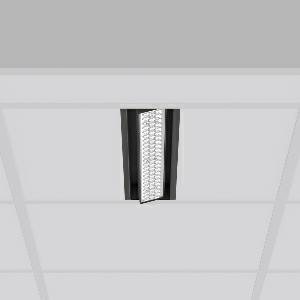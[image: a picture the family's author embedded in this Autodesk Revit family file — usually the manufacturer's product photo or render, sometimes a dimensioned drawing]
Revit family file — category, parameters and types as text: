
# Revit family: tx-move_901725_003_1_76_cce0
name_source: partatom
category: Lighting Fixtures
units: mm (PartAtom-declared; Revit-internal decimal feet)

## family parameters
Cut with Voids When Loaded = No
Host = Face
Light Source = No
Part Type = Normal
Room Calculation Point = No
Round Connector Dimension = Use Diameter
Shared = No

## types (1)
- MultiLumen 1 (1 x LED Modul 840, 3000 lm, 4000)
    Apparent Load = 18 VA
    Approval mark = CE
    CIE Flux Codes = 77 96 99 100 100
    Color Rendering = 80
    Color Temperature = 4000
    Default Elevation = 1800 mm
    Description = Series: TX-MOVE
Einlege/Einbau-Flächenstrahler. Housing: sheet steel, powder-coated. Swivel range: 90°. High-efficiency LED units with optimum light control thanks to clear plastic (PC) lens optics. Spezielle Mikrostrukturen reduzieren Gelbsaum. Symmetrical light distribution. Suitable for laying in grid ceiling module 600. Connected converter included in separate gearbox.Suitable for through-wiring.MultiLumen: Luminous flux adjustable in 3 steps. Accessories: Mounting frame for installation in suspended ceilings. Environmentally friendly and resource-saving due to replaceable and recyclable components. 
Colour: deep black, matt (RAL 9005)
Length: 597 mm
Width: 116 mm
Height: 39 mm
Cut-out length: 577 mm
Cut-out width: 98 mm
Recess height: 100 mm
Lamp: LED
Socket: without socket
Colour temperature: 4000K
Colour rendering index (CRI): 80
System power: 18 W
Rated luminous flux: 3000 lm
Luminous efficiency: 167 lm/W
System power 2: 26 W
Rated luminous flux 2: 4100 lm
Luminous efficiency 2: 158 lm/W
System power 3: 39 W
Rated luminous flux 3: 5800 lm
Luminous efficiency 3: 149 lm/W
Control gear: Dimmable EVG, DALI
Protection class: I
Type of protection: IP 20
    Height = 0 mm  [stored 0 ft]
    Lamp = 1 x LED Modul 840
    Lamp Light Flux = 3000 lm
    Lamp count = 1
    Length = 597 mm
    Lifetime = 50000 h
    Luminous efficacy = 167 lm/W
    Manufacturer = RZB
    ModVariant = No
    Model = 901725.003.1.76
    Mounting Place = Ceiling, Wall
    Mounting Type = Recessed
    Number of Poles = 1
    OnlyDefault = Yes
    Power Factor = 1
    Product Name = TX-MOVE
    Product group = Recessed projectors
    ProductGroupID = 401
    Protection Class = Protection class I
    Protection Degree = IP 20
    RLX_Detail_Level = 1
    RLX_Emergency_Light_Flux = 0 lm
    RLX_Emergency_Type = 0
    RLX_Emergency_Type_DB = No
    RlxData = <blob elided: 29425 chars, md5=da2f3526>
    Socket = socket
    Standby Power = 0 W
    System Light Flux = 3000 lm
    System Power = 18 W
    Type Comments = MultiLumen 1
    Type Image = 901725.003.jpg
    URL = http://relux.com
    VarID = multilumen_1
    Voltage = 230 V
    Voltage Range = 220-240 V
    Weight = 0.00 kg
    Width = 116 mm

note: [stored X ft] marks values corroborated as IEEE doubles in the binary element streams (Revit-internal decimal feet)

## geometry (parser evidence)
native form markers: Blend x4, Sweep x12
no freeform markers — native parametric forms only
